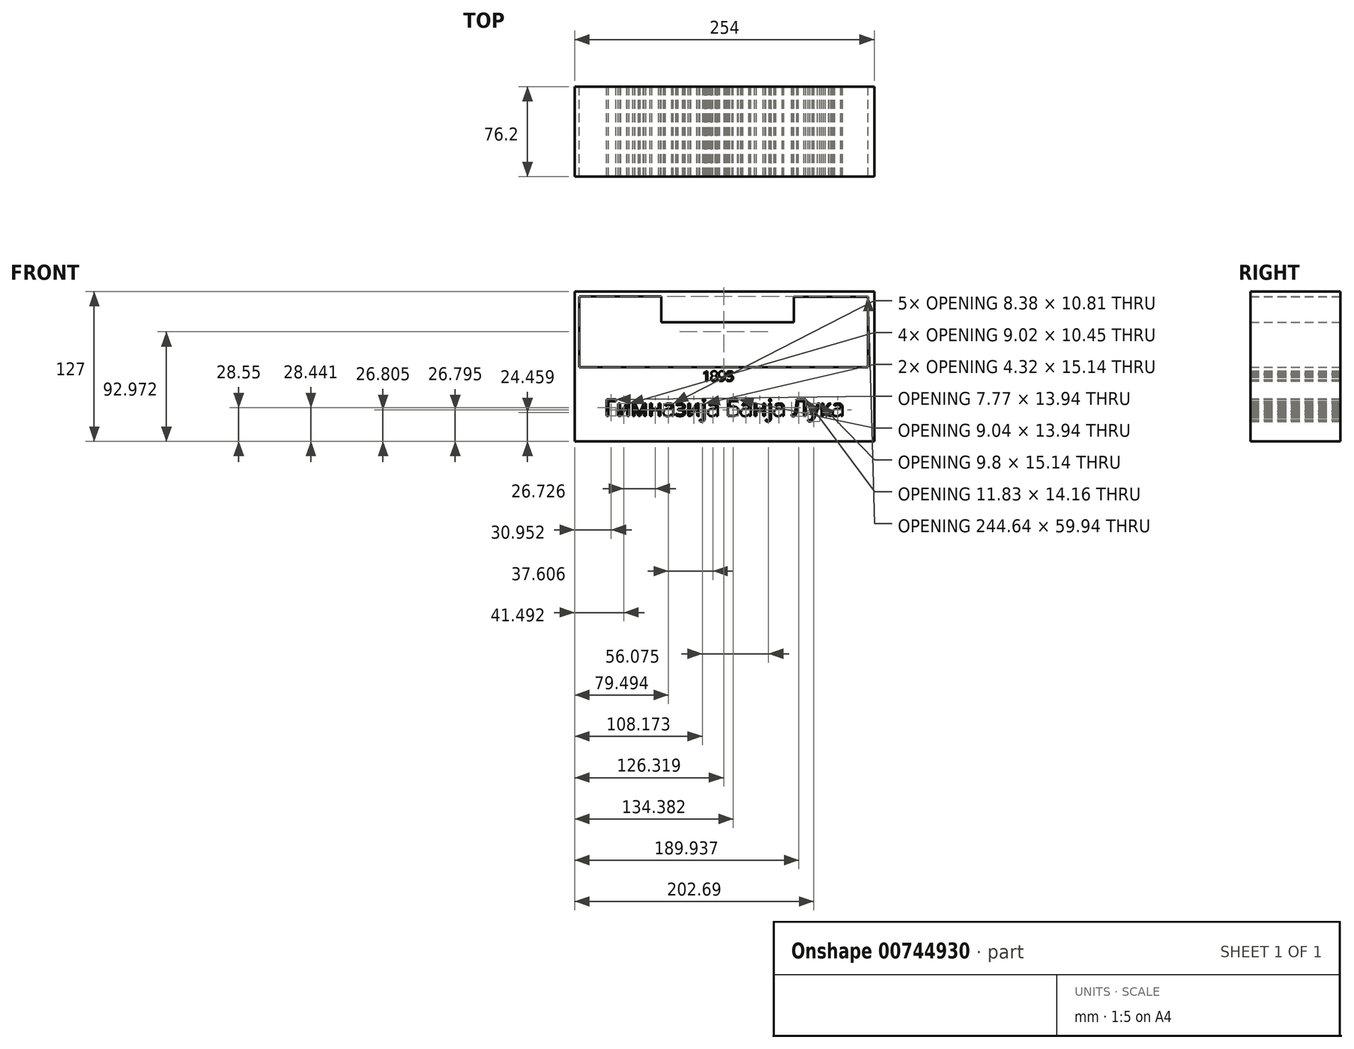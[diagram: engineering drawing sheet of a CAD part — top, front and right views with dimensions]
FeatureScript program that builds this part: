
annotation { "Feature Type Name" : "Feature", "Feature Type Description" : "" }
export const myFeature = defineFeature(function(context is Context, id is Id, definition is map)
    precondition{}
    {
        {
            var Q0;
            Q0=qCreatedBy(makeId("Front.planeOp"),FACE);
            var sketch = newSketch(context, id + "F0", { "sketchPlane" : qUnion([Q0])});
            skLineSegment(sketch, "E0.bottom", {"start": v(-145.88, 0) * mm, "end": v(108.12, 0) * mm});
            skLineSegment(sketch, "E0.top", {"start": v(-145.88, -127) * mm, "end": v(108.12, -127) * mm});
            skLineSegment(sketch, "E0.left", {"start": v(-145.88, 0) * mm, "end": v(-145.88, -127) * mm});
            skLineSegment(sketch, "E0.right", {"start": v(108.12, 0) * mm, "end": v(108.12, -127) * mm});
            skLineSegment(sketch, "E1.bottom", {"start": v(-141.88, -4.06) * mm, "end": v(-72.6, -4.06) * mm});
            skLineSegment(sketch, "E2.bottom", {"start": v(40.04, -4.37) * mm, "end": v(102.76, -4.37) * mm});
            skLineSegment(sketch, "E3.0", {"start": v(-145.88, -80.42) * mm, "end": v(108.12, -80.42) * mm});
            skLineSegment(sketch, "E4", {"start": v(-141.88, -64) * mm, "end": v(-72.6, -64) * mm});
            skLineSegment(sketch, "E5", {"start": v(102.76, -64) * mm, "end": v(-72.6, -64) * mm});
            skLineSegment(sketch, "E6", {"start": v(-141.88, -4.06) * mm, "end": v(-141.88, -64) * mm});
            skLineSegment(sketch, "E7", {"start": v(-72.6, -4.06) * mm, "end": v(-72.6, -64) * mm});
            skLineSegment(sketch, "E8", {"start": v(40.04, -4.37) * mm, "end": v(40.04, -64) * mm});
            skLineSegment(sketch, "E9", {"start": v(102.76, -4.37) * mm, "end": v(102.76, -64) * mm});
            skText(sketch, "E10", { "text": "1895", "fontName": "OpenSans-Regular.ttf"});
            skText(sketch, "E11", { "text": "Гимназија Банја Лука", "fontName": "OpenSans-Regular.ttf"});
            skLineSegment(sketch, "E12", {"start": v(-72.6, -25.93) * mm, "end": v(40.04, -25.93) * mm});
            skLineSegment(sketch, "E13", {"start": v(40.04, -25.93) * mm, "end": v(40.04, -57.15) * mm});
            skLineSegment(sketch, "E14", {"start": v(40.04, -57.15) * mm, "end": v(-72.6, -57.15) * mm});
            skLineSegment(sketch, "E15", {"start": v(-72.6, -25.93) * mm, "end": v(-90, -25.93) * mm});
            skLineSegment(sketch, "E16", {"start": v(-72.6, -57.15) * mm, "end": v(-90, -57.15) * mm});
            skLineSegment(sketch, "E17", {"start": v(57.2, -25.93) * mm, "end": v(57.2, -57.15) * mm});
            skLineSegment(sketch, "E18", {"start": v(57.2, -25.93) * mm, "end": v(40.04, -25.93) * mm});
            skLineSegment(sketch, "E19", {"start": v(57.2, -57.15) * mm, "end": v(40.04, -57.15) * mm});
            skLineSegment(sketch, "E20", {"start": v(-90, -25.93) * mm, "end": v(-90, -57.15) * mm});
            skLineSegment(sketch, "E21", {"start": v(-145.88, -87.12) * mm, "end": v(108.12, -87.12) * mm});
            const initialGuessF0  = {"E10": [-0.03765, -0.07588, 1, 0, 0.0084], "E11": [-0.12073, -0.10542, 1, 0, 0.01406]};
            skSetInitialGuess(sketch, initialGuessF0);
            skSolve(sketch);
        }
        {
            var Q0;
            Q0 = qSketchRegion(id + "F0", true);
            extrude(context, id + "F1", {"entities" : qUnion([Q0]), "endBound" : BoundingType.SYMMETRIC, "depth" : 76.2 * mm, "offsetDistance" : 25.4 * mm});
        }
    });
